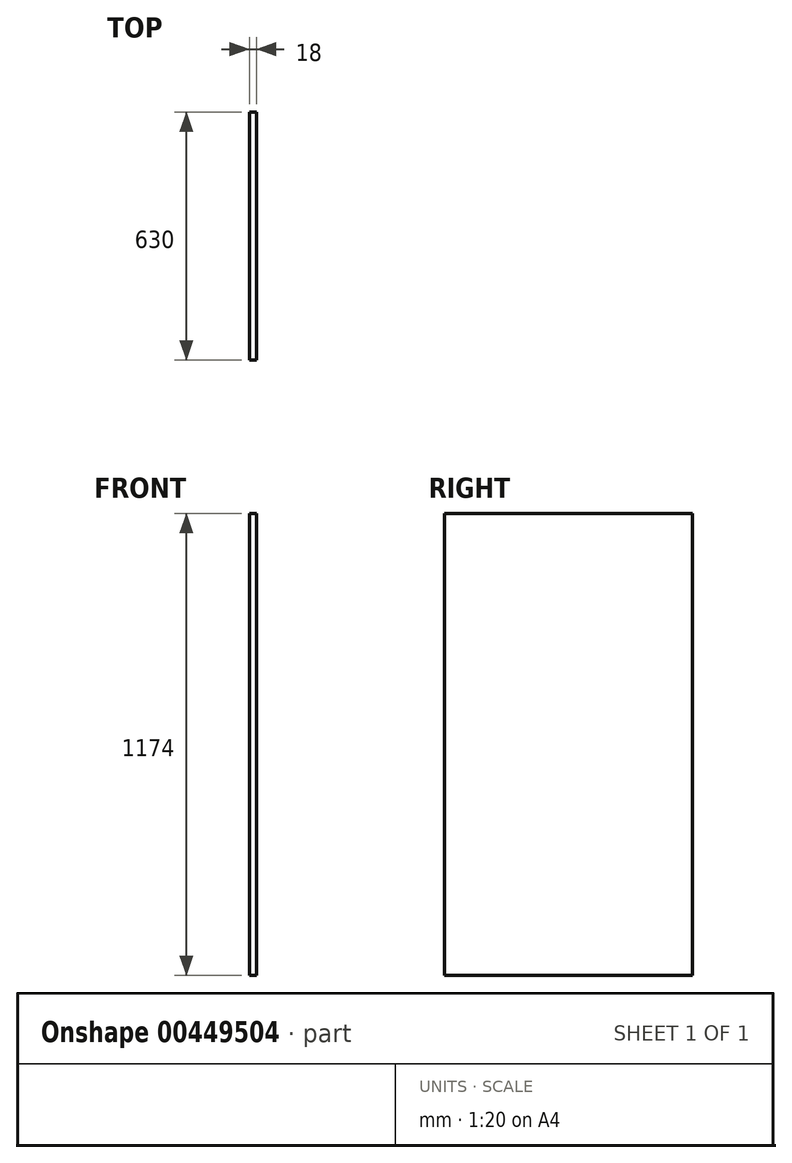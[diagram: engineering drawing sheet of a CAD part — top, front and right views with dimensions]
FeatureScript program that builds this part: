
annotation { "Feature Type Name" : "Feature", "Feature Type Description" : "" }
export const myFeature = defineFeature(function(context is Context, id is Id, definition is map)
    precondition{}
    {
        {
            var Q0;
            Q0=qCreatedBy(makeId("Right.planeOp"),FACE);
            var sketch = newSketch(context, id + "F0", { "sketchPlane" : qUnion([Q0])});
            skLineSegment(sketch, "E0.bottom", {"start": v(0, 1174) * mm, "end": v(630, 1174) * mm});
            skLineSegment(sketch, "E0.top", {"start": v(0, 0) * mm, "end": v(630, 0) * mm});
            skLineSegment(sketch, "E0.left", {"start": v(0, 1174) * mm, "end": v(0, 0) * mm});
            skLineSegment(sketch, "E0.right", {"start": v(630, 1174) * mm, "end": v(630, 0) * mm});
            skSolve(sketch);
        }
        {
            var Q0;
            Q0 = qSketchRegion(id + "F0", true);
            extrude(context, id + "F1", {"entities" : qUnion([Q0]), "oppositeDirection" : true, "depth" : 18 * mm});
        }
    });
